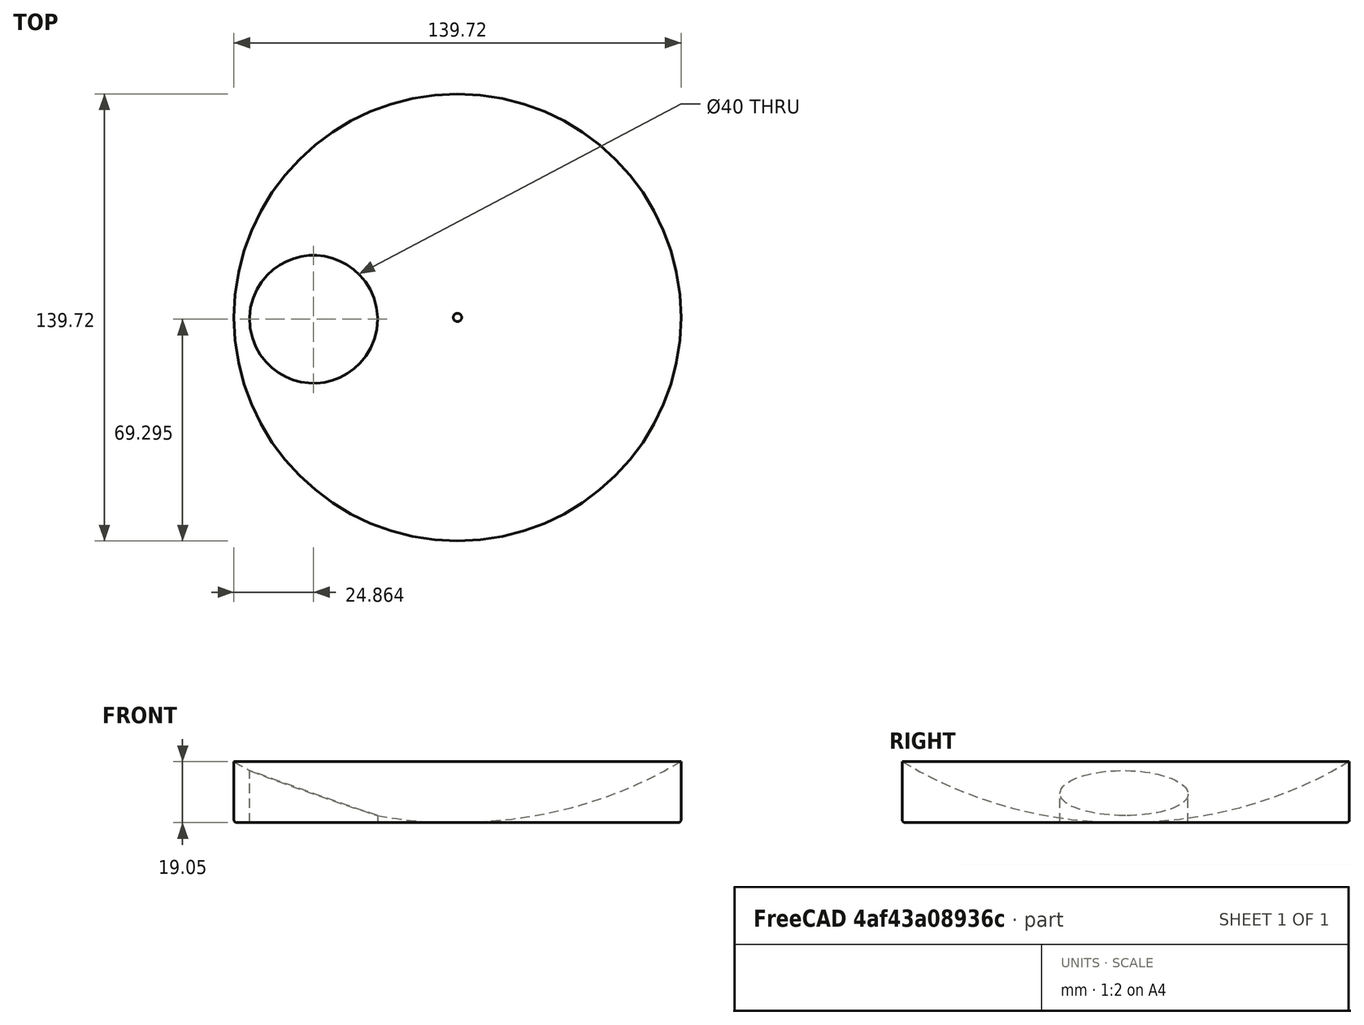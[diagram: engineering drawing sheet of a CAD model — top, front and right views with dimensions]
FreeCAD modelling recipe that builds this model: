
FCSTD DOCUMENT  (FreeCAD 0.17R13541 (Git))
Label: speaker_platform
License: All rights reserved
LicenseURL: http://en.wikipedia.org/wiki/All_rights_reserved
objects: Sketcher::SketchObject×2, PartDesign::Revolution×1, PartDesign::Pocket×1, PartDesign::Body×1
note: 7 computed .brp shape members not serialized (recipe doc carries the construction recipe); baked Part::Feature solids carry a one-line shape summary decoded from their .brp

FEATURE [Sketcher::SketchObject] Sketch
  MapMode = 5
  Support = -> [XY_Plane]
  sketch-geometry (1):
    g0: Circle CenterX=-44.9965 CenterY=-0.565161 CenterZ=0 NormalX=0 NormalY=0 NormalZ=1 AngleXU=0 Radius=20
  constraints (1):
    c: Radius(g0) = 20
FEATURE [Sketcher::SketchObject] Sketch001
  MapMode = 5
  Placement = pos=(0,0,0) rot=(1,0,0;1.5708rad)
  Support = -> [XZ_Plane]
  sketch-geometry (4):
    g0: LineSegment StartX=-69.8627 StartY=1.02055 StartZ=0 EndX=-69.8627 EndY=19.1913 EndZ=0
    g1: LineSegment StartX=-68.9831 StartY=0.140929 StartZ=0 EndX=0 EndY=0.140929 EndZ=0
    g2: ArcOfCircle CenterX=-0.652874 CenterY=135.374 CenterZ=0 NormalX=0 NormalY=0 NormalZ=1 AngleXU=0 Radius=135.235 StartAngle=4.17514 EndAngle=4.71722
    g3: ArcOfCircle CenterX=-68.9831 CenterY=1.02055 CenterZ=0 NormalX=0 NormalY=0 NormalZ=1 AngleXU=0 Radius=0.879623 StartAngle=3.14159 EndAngle=4.71239
  constraints (7):
    c: Vertical(g0)
    c: Horizontal(g1)
    c: DistanceX(g1,g-1) = 0
    c: Coincident(g0,g2)
    c: Coincident(g2,g1)
    c: Tangent(g1,g3) = -1.5708
    c: Tangent(g0,g3) = 1.5708
FEATURE [PartDesign::Revolution] Revolution
  Angle = 360
  Axis = (0,0,1)
  Base = (0,0,0)
  Placement = pos=(0,0,0) rot=(1,0,0;1.5708rad)
  Profile = -> Sketch001
  ReferenceAxis = -> Sketch001 [V_Axis]
FEATURE [PartDesign::Pocket] Pocket
  BaseFeature = -> Revolution
  Length = 50
  Length2 = 100
  Midplane = true
  Placement = pos=(0,0,0) rot=(1,0,0;1.5708rad)
  Profile = -> Sketch
  Type = 0
FEATURE [PartDesign::Body] Body  label="Speaker Platform"
  Group = -> [Sketch,Sketch001,Revolution,Pocket]
  Origin = -> Origin
  Tip = -> Pocket
